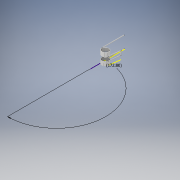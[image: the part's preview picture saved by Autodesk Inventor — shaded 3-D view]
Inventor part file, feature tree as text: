
AUTODESK INVENTOR PART (.ipt)
format: ipt  version: 2018 (Build 220112000, 112)  size: 366,080 bytes
history: native  units: in
note: dims shown in document units (in); Inventor stores cm internally (conversion verified against a paired STEP export)
features: sketch x12, extrude x10, projected_geometry x8, helix x1, mirror x1
ambient origin geometry x8: Origin, YZ Plane, XZ Plane, XY Plane, X Axis, Y Axis, Z Axis, Center Point
bodies: Solid1 (feature_tree)
feature tree (32):
  helix  "Coil1"  [1 undecoded]
  extrude  "Extrusion1"  Depth=1.3in TaperAngle=0.0deg
  extrude  "Extrusion2"  Depth=0.0225in
  extrude  "Extrusion9"  Depth=0.35in TaperAngle=0.0deg
  extrude  "Extrusion10"  Depth=1.0in TaperAngle=0.0deg
  extrude  "Extrusion11"  Depth=0.0225in
  mirror  "Mirror2"
  sketch  "Sketch13"  dims[d45=1.0in d46=0.0in d47=1.0in d48=0.0in]
  extrude  "Extrusion12"  Depth=1.0in TaperAngle=0.0deg
  extrude  "Extrusion13"  Depth=1.0in TaperAngle=0.0deg
  extrude  "Extrusion14"  [1 undecoded]
  extrude  "Extrusion15"  [1 undecoded]
  extrude  "Extrusion16"  [1 undecoded]
  sketch  "Sketch1"  dims[d1=0.215in]
  sketch  "Sketch2"  dims[d2=0.23in d3=0.23in d4=1.7638in d5=0.0in d6=90.0deg d7=90.0deg d8=0.0in d9=0.0in d10=1.3in d11=0.0in]
  projected_geometry  "Projected Loop1"
  sketch  "Sketch3"  dims[d12=0.7in d13=0.0in d32=0.0225in]
  sketch  "Sketch10"  dims[d33=0.35in d34=0.0in d35=0.35in d36=0.0in]
  projected_geometry  "Projected Loop5"
  sketch  "Sketch11"  dims[d37=0.35in d38=0.0in d41=1.0in d42=0.0in]
  projected_geometry  "Projected Loop6"
  sketch  "Sketch12"  dims[d43=0.0225in d44=0.0225in]
  projected_geometry  "Projected Loop7"
  projected_geometry  "Projected Loop8"
  sketch  "Sketch14"  dims[d49=1.0in d50=0.0in d51=1.0in d52=0.0in]
  projected_geometry  "Projected Loop9"
  sketch  "Sketch15"  dims[d53=1.1874in]
  sketch  "Sketch16"
  projected_geometry  "Projected Loop10"
  sketch  "Sketch17"
  projected_geometry  "Projected Loop11"
  sketch  "Sketch18"
note: 4 required parameter values undecoded (feature->parameter linkage not recoverable at this tier; creation-order binding heuristic only, values carry confidence <= 0.55)
